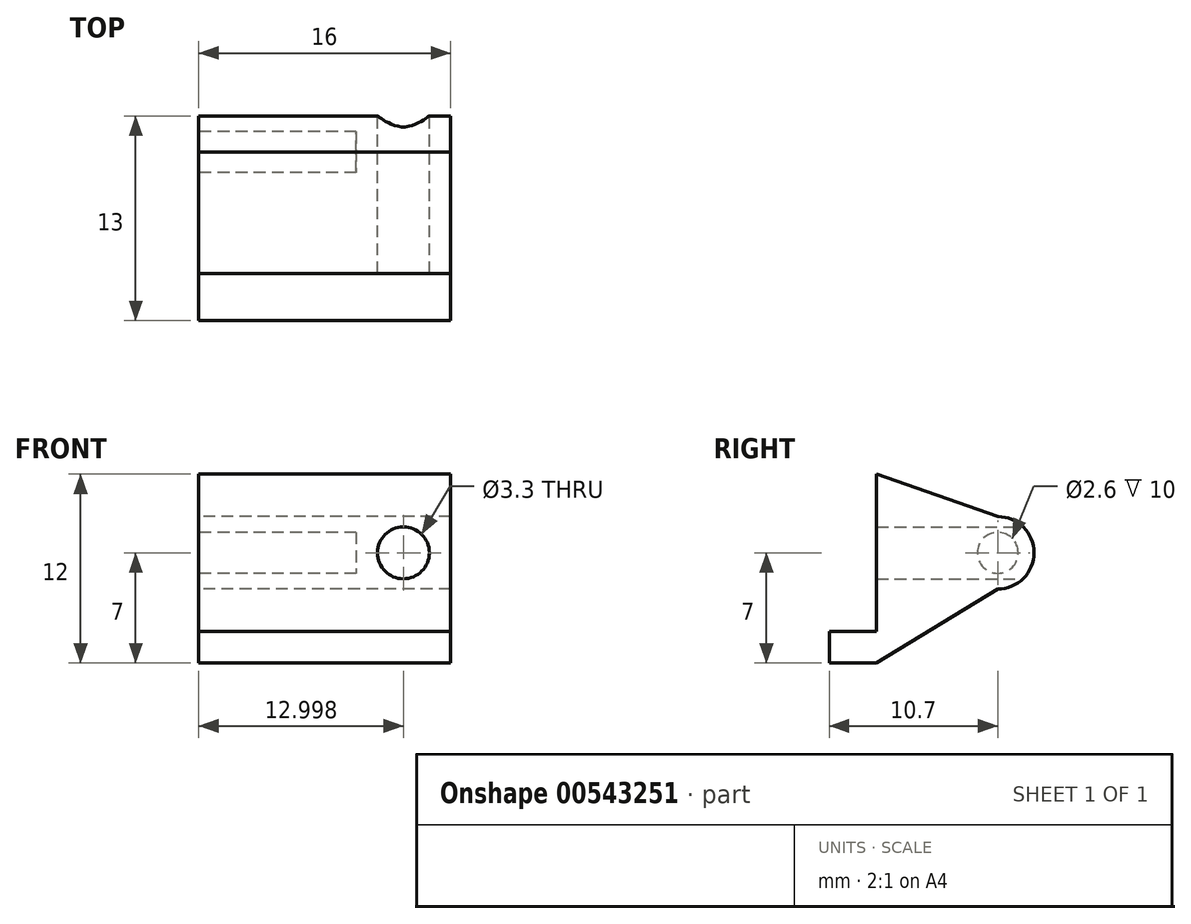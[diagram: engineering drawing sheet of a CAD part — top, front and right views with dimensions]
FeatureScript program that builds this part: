
annotation { "Feature Type Name" : "Feature", "Feature Type Description" : "" }
export const myFeature = defineFeature(function(context is Context, id is Id, definition is map)
    precondition{}
    {
        {
            var Q0;
            Q0=qCreatedBy(makeId("Front.planeOp"),FACE);
            var sketch = newSketch(context, id + "F0", { "sketchPlane" : qUnion([Q0])});
            skLineSegment(sketch, "E0.bottom", {"start": v(-13.95, 5) * mm, "end": v(2.05, 5) * mm});
            skLineSegment(sketch, "E0.top", {"start": v(-13.95, -7) * mm, "end": v(2.05, -7) * mm});
            skLineSegment(sketch, "E0.left", {"start": v(-13.95, 5) * mm, "end": v(-13.95, -7) * mm});
            skLineSegment(sketch, "E0.right", {"start": v(2.05, 5) * mm, "end": v(2.05, -7) * mm});
            skCircle(sketch, "E1", {"center": v(-0.95, 0) * mm, "radius": 1.65 * mm});
            skSolve(sketch);
        }
        {
            var Q0;
            Q0=makeQuery(id+"F0.imprint","IMPRINT",FACE,{"disambiguationData":[TD([[makeQuery(id+"F0.imprint","IMPRINT",EDGE,{"derivedFrom":sQuery(id+"F0.wireOp",EDGE,"E0.bottom")}),-1.0]])]});
            extrude(context, id + "F1", {"entities" : qUnion([Q0]), "depth" : 13 * mm, "offsetDistance" : 25 * mm});
        }
        {
            var Q0;
            Q0=makeQuery(id+"F1.opExtrude","CAP_FACE",FACE,{"disambiguationData":[OSD([sQuery(id+"F0.wireOp",EDGE,"E0.bottom"),sQuery(id+"F0.wireOp",EDGE,"E0.top"),sQuery(id+"F0.wireOp",EDGE,"E0.left"),sQuery(id+"F0.wireOp",EDGE,"E0.right"),sQuery(id+"F0.wireOp",EDGE,"E1")])],"isStart":false});
            var sketch = newSketch(context, id + "F2", { "sketchPlane" : qUnion([Q0])});
            skLineSegment(sketch, "E2", {"start": v(-13.95, -5) * mm, "end": v(2.05, -5) * mm});
            skLineSegment(sketch, "E3", {"start": v(2.05, -5) * mm, "end": v(2.05, -7) * mm});
            skLineSegment(sketch, "E4", {"start": v(2.05, -7) * mm, "end": v(-13.95, -7) * mm});
            skLineSegment(sketch, "E5", {"start": v(-13.95, -7) * mm, "end": v(-13.95, -5) * mm});
            skSolve(sketch);
        }
        {
            var Q0;
            {var subQ2=sQuery(id+"F2.wireOp",EDGE,"E2");Q0=makeQuery(id+"F2.imprint","IMPRINT",FACE,{"disambiguationData":[TD([[makeQuery(id+"F2.imprint","IMPRINT",EDGE,{"derivedFrom":subQ2}),1.0]])]});}
            extrude(context, id + "F3", {"entities" : qUnion([Q0]), "operationType" : NewBodyOperationType.REMOVE, "oppositeDirection" : true, "depth" : 3 * mm, "offsetDistance" : 25 * mm});
        }
        {
            var Q0;
            Q0=makeQuery(id+"F1.opExtrude","SWEPT_FACE",FACE,{"disambiguationData":[OSD([sQuery(id+"F0.wireOp",EDGE,"E0.left")])]});
            var sketch = newSketch(context, id + "F4", { "sketchPlane" : qUnion([Q0])});
            skCircle(sketch, "E6", {"center": v(2.3, 0) * mm, "radius": 1.3 * mm});
            skCircle(sketch, "E7", {"center": v(2.3, 0) * mm, "radius": 2.3 * mm});
            skLineSegment(sketch, "E8", {"start": v(2.3, 2.3) * mm, "end": v(10, 5) * mm});
            skLineSegment(sketch, "E9", {"start": v(2.3, -2.3) * mm, "end": v(10, -7) * mm});
            skSolve(sketch);
        }
        {
            var Q0;
            {var subQ0=sQuery(id+"F4.wireOp",EDGE,"E8");Q0=makeQuery(id+"F4.imprint","IMPRINT",FACE,{"disambiguationData":[TD([[makeQuery(id+"F4.imprint","IMPRINT",EDGE,{"derivedFrom":subQ0}),1.0]])]});}
            var Q1;
            {var subQ0=sQuery(id+"F4.wireOp",EDGE,"E9");Q1=makeQuery(id+"F4.imprint","IMPRINT",FACE,{"disambiguationData":[TD([[makeQuery(id+"F4.imprint","IMPRINT",EDGE,{"derivedFrom":subQ0}),-1.0]])]});}
            extrude(context, id + "F5", {"entities" : qUnion([Q0, Q1]), "operationType" : NewBodyOperationType.REMOVE, "endBound" : BoundingType.THROUGH_ALL, "oppositeDirection" : true, "depth" : 25 * mm, "offsetDistance" : 25 * mm});
        }
        {
            var Q0;
            Q0=makeQuery(id+"F1.opExtrude","SWEPT_FACE",FACE,{"disambiguationData":[OSD([sQuery(id+"F0.wireOp",EDGE,"E0.left")])]});
            var sketch = newSketch(context, id + "F6", { "sketchPlane" : qUnion([Q0])});
            skCircle(sketch, "E10", {"center": v(2.3, 0) * mm, "radius": 1.3 * mm});
            skSolve(sketch);
        }
        {
            var Q0;
            Q0=makeQuery(id+"F6.imprint","IMPRINT",FACE,{"disambiguationData":[TD([[makeQuery(id+"F6.imprint","IMPRINT",EDGE,{"derivedFrom":sQuery(id+"F6.wireOp",EDGE,"E10")}),1.0]])]});
            extrude(context, id + "F7", {"entities" : qUnion([Q0]), "operationType" : NewBodyOperationType.REMOVE, "oppositeDirection" : true, "depth" : 10 * mm, "offsetDistance" : 25 * mm});
        }
    });
